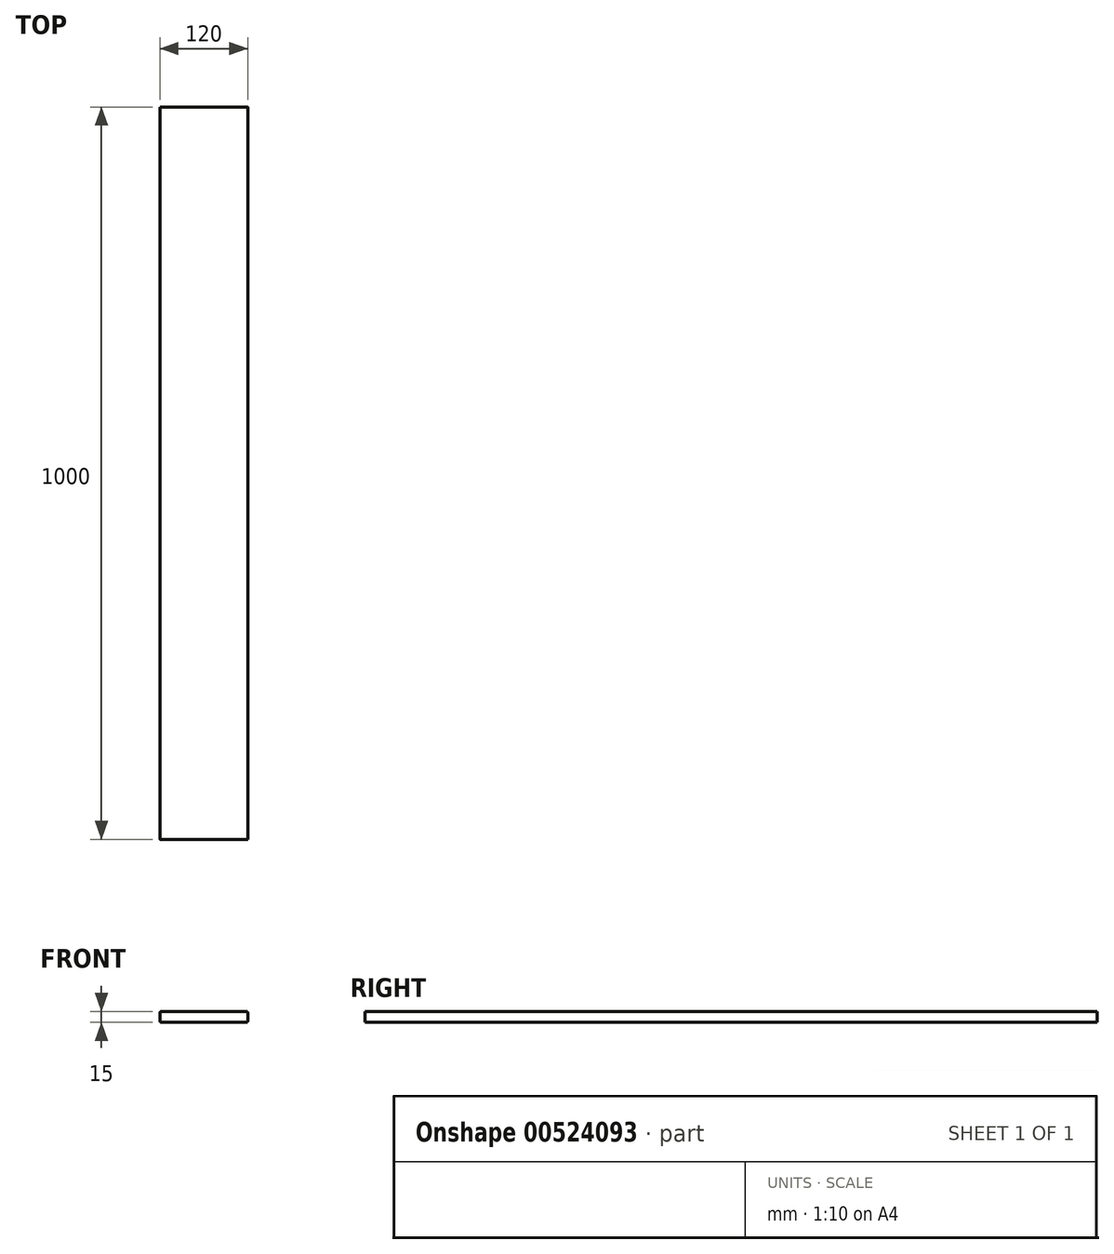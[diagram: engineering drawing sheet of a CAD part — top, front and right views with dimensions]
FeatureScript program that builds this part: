
annotation { "Feature Type Name" : "Feature", "Feature Type Description" : "" }
export const myFeature = defineFeature(function(context is Context, id is Id, definition is map)
    precondition{}
    {
        {
            var Q0;
            Q0=qCreatedBy(makeId("Front.planeOp"),FACE);
            var sketch = newSketch(context, id + "F0", { "sketchPlane" : qUnion([Q0])});
            skLineSegment(sketch, "E0.bottom", {"start": v(-60, 7.5) * mm, "end": v(60, 7.5) * mm});
            skLineSegment(sketch, "E0.top", {"start": v(-60, -7.5) * mm, "end": v(60, -7.5) * mm});
            skLineSegment(sketch, "E0.left", {"start": v(-60, 7.5) * mm, "end": v(-60, -7.5) * mm});
            skLineSegment(sketch, "E0.right", {"start": v(60, 7.5) * mm, "end": v(60, -7.5) * mm});
            skSolve(sketch);
        }
        {
            var Q0;
            Q0 = qSketchRegion(id + "F0", true);
            extrude(context, id + "F1", {"entities" : qUnion([Q0]), "endBound" : BoundingType.SYMMETRIC, "depth" : 1000 * mm, "offsetDistance" : 25 * mm});
        }
        {
            var Q0;
            Q0=makeQuery(id+"F1.opExtrude","SWEPT_EDGE",EDGE,{"disambiguationData":[OSD([sQuery(id+"F0.wireOp",EDGE,"E0.bottom"),sQuery(id+"F0.wireOp",EDGE,"E0.right")])]});
            var Q1;
            Q1=makeQuery(id+"F1.opExtrude","SWEPT_EDGE",EDGE,{"disambiguationData":[OSD([sQuery(id+"F0.wireOp",EDGE,"E0.top"),sQuery(id+"F0.wireOp",EDGE,"E0.right")])]});
            var Q2;
            Q2=makeQuery(id+"F1.opExtrude","SWEPT_EDGE",EDGE,{"disambiguationData":[OSD([sQuery(id+"F0.wireOp",EDGE,"E0.top"),sQuery(id+"F0.wireOp",EDGE,"E0.left")])]});
            var Q3;
            Q3=makeQuery(id+"F1.opExtrude","SWEPT_EDGE",EDGE,{"disambiguationData":[OSD([sQuery(id+"F0.wireOp",EDGE,"E0.bottom"),sQuery(id+"F0.wireOp",EDGE,"E0.left")])]});
            fillet(context, id + "F2", {"entities" : qUnion([Q0, Q1, Q2, Q3]), "radius" : 2 * mm, "tangentPropagation" : true, "allowEdgeOverflow" : false});
        }
    });
